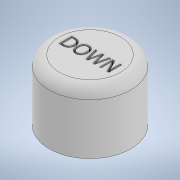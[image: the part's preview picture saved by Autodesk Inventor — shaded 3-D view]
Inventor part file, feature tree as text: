
AUTODESK INVENTOR PART (.ipt)
format: ipt  version: 2021 (Build 250183000, 183)  size: 200,704 bytes
history: native  units: mm
features: extrude x3, sketch x3, fillet x1
ambient origin geometry x8: Origin, YZ Plane, XZ Plane, XY Plane, X Axis, Y Axis, Z Axis, Center Point
bodies: Solid1 (feature_tree)
feature tree (7):
  extrude  "Extrusion1"  Depth=15.0mm TaperAngle=0.0deg
  fillet  "Fillet1"  Radius=2.5mm
  extrude  "Extrusion2"  Depth=2.5mm TaperAngle=0.0deg
  extrude  "Extrusion3"  [1 undecoded]
  sketch  "Sketch1"  dims[d0=20.0mm d1=15.0mm d2=0.0mm d3=2.5mm]
  sketch  "Sketch2"  dims[d4=5.0mm d5=0.0mm d6=2.5mm d7=0.0mm]
  sketch  "Sketch3"
note: 1 required parameter value undecoded (feature->parameter linkage not recoverable at this tier; creation-order binding heuristic only, values carry confidence <= 0.55)
